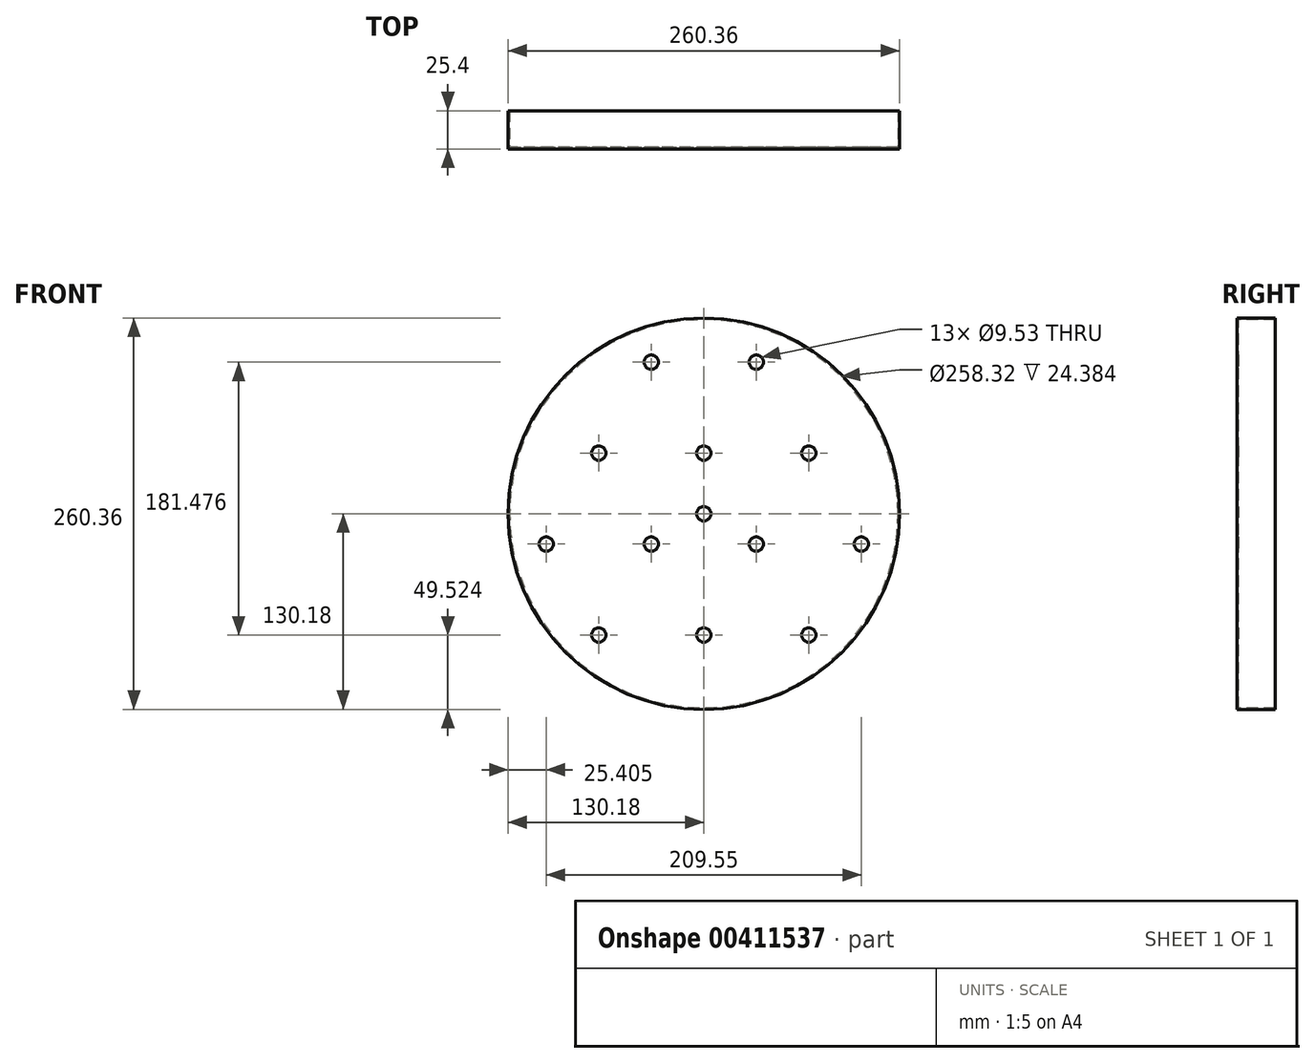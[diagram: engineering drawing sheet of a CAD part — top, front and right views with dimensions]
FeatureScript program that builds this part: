
annotation { "Feature Type Name" : "Feature", "Feature Type Description" : "" }
export const myFeature = defineFeature(function(context is Context, id is Id, definition is map)
    precondition{}
    {
        {
            var Q0;
            Q0=qCreatedBy(makeId("Top.planeOp"),FACE);
            var sketch = newSketch(context, id + "F0", { "sketchPlane" : qUnion([Q0])});
            skLineSegment(sketch, "E0.bottom", {"start": v(0, 0) * mm, "end": v(130.18, 0) * mm});
            skLineSegment(sketch, "E0.top", {"start": v(0, 1.02) * mm, "end": v(129.16, 1.02) * mm});
            skLineSegment(sketch, "E0.left", {"start": v(0, 0) * mm, "end": v(0, 1.02) * mm});
            skLineSegment(sketch, "E1.top", {"start": v(130.18, 25.4) * mm, "end": v(129.16, 25.4) * mm});
            skLineSegment(sketch, "E1.right", {"start": v(129.16, 1.02) * mm, "end": v(129.16, 25.4) * mm});
            skLineSegment(sketch, "E2", {"start": v(130.18, 25.4) * mm, "end": v(130.18, 0) * mm});
            skSolve(sketch);
        }
        {
            var Q0;
            Q0=makeQuery(id+"F0.imprint","IMPRINT",FACE,{"disambiguationData":[TD([[makeQuery(id+"F0.imprint","IMPRINT",EDGE,{"derivedFrom":sQuery(id+"F0.wireOp",EDGE,"E0.bottom")}),1.0]])]});
            var Q1;
            Q1=sQuery(id+"F0.wireOp",EDGE,"E0.left");
            revolve(context, id + "F1", {"entities" : qUnion([Q0]), "axis" : qUnion([Q1]), "revolveType" : RevolveType.FULL});
        }
        {
            var Q0;
            Q0=makeQuery(id+"F1.opRevolve","SWEPT_FACE",FACE,{"disambiguationData":[OSD([sQuery(id+"F0.wireOp",EDGE,"E0.top")])]});
            var sketch = newSketch(context, id + "F2", { "sketchPlane" : qUnion([Q0])});
            skCircle(sketch, "E3", {"center": v(0, 0) * mm, "radius": 4.76 * mm});
            skCircle(sketch, "E4", {"center": v(-69.85, 40.33) * mm, "radius": 4.76 * mm});
            skCircle(sketch, "E5", {"center": v(-69.85, 40.33) * mm, "radius": 34.93 * mm, "construction": true});
            skCircle(sketch, "E6", {"center": v(-34.93, -20.16) * mm, "radius": 4.76 * mm});
            skCircle(sketch, "E7", {"center": v(-34.93, -20.16) * mm, "radius": 34.93 * mm, "construction": true});
            skCircle(sketch, "E8", {"center": v(34.92, -20.16) * mm, "radius": 4.76 * mm});
            skCircle(sketch, "E9", {"center": v(34.92, -20.16) * mm, "radius": 34.93 * mm, "construction": true});
            skCircle(sketch, "E10", {"center": v(0, 40.33) * mm, "radius": 4.76 * mm});
            skCircle(sketch, "E11", {"center": v(0, 40.33) * mm, "radius": 34.93 * mm, "construction": true});
            skCircle(sketch, "E12", {"center": v(-34.92, 100.82) * mm, "radius": 4.76 * mm});
            skCircle(sketch, "E13", {"center": v(-34.92, 100.82) * mm, "radius": 34.93 * mm, "construction": true});
            skCircle(sketch, "E14", {"center": v(-104.78, -20.16) * mm, "radius": 4.76 * mm});
            skCircle(sketch, "E15", {"center": v(-104.78, -20.16) * mm, "radius": 34.93 * mm, "construction": true});
            skCircle(sketch, "E16", {"center": v(34.92, 100.82) * mm, "radius": 4.76 * mm});
            skCircle(sketch, "E17", {"center": v(34.92, 100.82) * mm, "radius": 34.93 * mm, "construction": true});
            skCircle(sketch, "E18", {"center": v(69.85, 40.33) * mm, "radius": 4.76 * mm});
            skCircle(sketch, "E19", {"center": v(69.85, 40.33) * mm, "radius": 34.93 * mm, "construction": true});
            skCircle(sketch, "E20", {"center": v(0, -80.66) * mm, "radius": 4.76 * mm});
            skCircle(sketch, "E21", {"center": v(0, -80.66) * mm, "radius": 34.93 * mm, "construction": true});
            skCircle(sketch, "E22", {"center": v(-69.85, -80.66) * mm, "radius": 4.76 * mm});
            skCircle(sketch, "E23", {"center": v(-69.85, -80.66) * mm, "radius": 34.93 * mm, "construction": true});
            skCircle(sketch, "E24", {"center": v(69.85, -80.66) * mm, "radius": 4.76 * mm});
            skCircle(sketch, "E25", {"center": v(69.85, -80.66) * mm, "radius": 34.93 * mm, "construction": true});
            skCircle(sketch, "E26", {"center": v(104.78, -20.16) * mm, "radius": 4.76 * mm});
            skCircle(sketch, "E27", {"center": v(104.78, -20.16) * mm, "radius": 34.93 * mm, "construction": true});
            skLineSegment(sketch, "E28", {"start": v(0, 40.33) * mm, "end": v(0, 0) * mm, "construction": true});
            skLineSegment(sketch, "E29", {"start": v(0, 0) * mm, "end": v(-34.93, -20.16) * mm, "construction": true});
            skLineSegment(sketch, "E30", {"start": v(0, 0) * mm, "end": v(34.93, -20.16) * mm, "construction": true});
            skSolve(sketch);
        }
        {
            var Q0;
            Q0=qSketchRegion(id+"F2",true);
            extrude(context, id + "F3", {"entities" : qUnion([Q0]), "operationType" : NewBodyOperationType.REMOVE, "endBound" : BoundingType.THROUGH_ALL, "oppositeDirection" : true, "depth" : 25.4 * mm});
        }
    });
